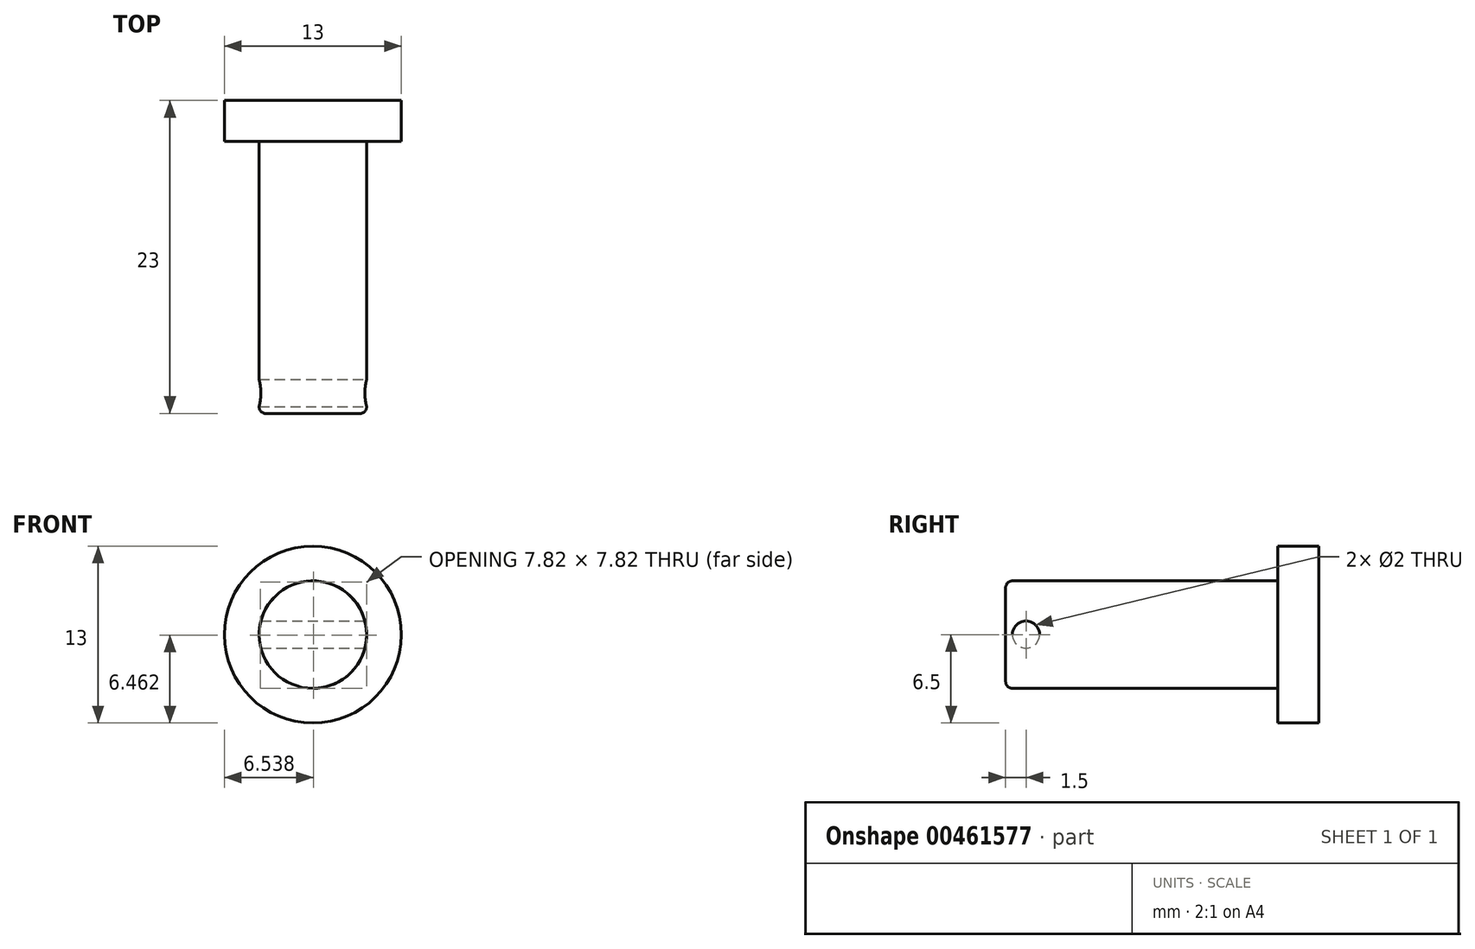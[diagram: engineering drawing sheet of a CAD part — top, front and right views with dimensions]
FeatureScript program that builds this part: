
annotation { "Feature Type Name" : "Feature", "Feature Type Description" : "" }
export const myFeature = defineFeature(function(context is Context, id is Id, definition is map)
    precondition{}
    {
        {
            var Q0;
            Q0=qCreatedBy(makeId("Front.planeOp"),FACE);
            var sketch = newSketch(context, id + "F0", { "sketchPlane" : qUnion([Q0])});
            skCircle(sketch, "E0", {"center": v(0, 0) * mm, "radius": 6.5 * mm});
            skSolve(sketch);
        }
        {
            var Q0;
            Q0=makeQuery(id+"F0.imprint","IMPRINT",FACE,{"disambiguationData":[TD([[makeQuery(id+"F0.imprint","IMPRINT",EDGE,{"derivedFrom":sQuery(id+"F0.wireOp",EDGE,"E0")}),1.0]])]});
            extrude(context, id + "F1", {"entities" : qUnion([Q0]), "depth" : 3 * mm});
        }
        {
            var Q0;
            Q0=makeQuery(id+"F1.opExtrude","CAP_FACE",FACE,{"disambiguationData":[OSD([sQuery(id+"F0.wireOp",EDGE,"E0")])],"isStart":false});
            var sketch = newSketch(context, id + "F2", { "sketchPlane" : qUnion([Q0])});
            skCircle(sketch, "E1", {"center": v(0, 0) * mm, "radius": 3.95 * mm});
            skSolve(sketch);
        }
        {
            var Q0;
            Q0=makeQuery(id+"F2.imprint","IMPRINT",FACE,{"disambiguationData":[TD([[makeQuery(id+"F2.imprint","IMPRINT",EDGE,{"derivedFrom":sQuery(id+"F2.wireOp",EDGE,"E1")}),1.0]])]});
            extrude(context, id + "F3", {"entities" : qUnion([Q0]), "operationType" : NewBodyOperationType.ADD, "depth" : 20 * mm});
        }
        {
            var Q0;
            Q0=qCreatedBy(makeId("Right.planeOp"),FACE);
            cPlane(context, id + "F4", {"entities" : qUnion([Q0]), "cplaneType" : CPlaneType.OFFSET, "offset" : 3.95 * mm, "width" : 150 * mm, "height" : 150 * mm});
        }
        {
            var Q0;
            Q0=qCreatedBy(id+"F4.planeOp",FACE);
            var sketch = newSketch(context, id + "F5", { "sketchPlane" : qUnion([Q0])});
            skCircle(sketch, "E2", {"center": v(-21.5, 0) * mm, "radius": 1 * mm});
            skSolve(sketch);
        }
        {
            var Q0;
            Q0=makeQuery(id+"F5.imprint","IMPRINT",FACE,{"disambiguationData":[TD([[makeQuery(id+"F5.imprint","IMPRINT",EDGE,{"derivedFrom":sQuery(id+"F5.wireOp",EDGE,"E2")}),1.0]])]});
            extrude(context, id + "F6", {"entities" : qUnion([Q0]), "operationType" : NewBodyOperationType.REMOVE, "endBound" : BoundingType.THROUGH_ALL, "oppositeDirection" : true, "depth" : 25 * mm});
        }
        {
            var Q0;
            Q0=makeQuery(id+"F3.opExtrude","CAP_EDGE",EDGE,{"disambiguationData":[OSD([sQuery(id+"F2.wireOp",EDGE,"E1")])],"isStart":false});
            fillet(context, id + "F7", {"entities" : qUnion([Q0]), "radius" : 0.5 * mm, "tangentPropagation" : true, "allowEdgeOverflow" : false});
        }
        {
            var Q0;
            Q0=makeQuery(id+"F1.opExtrude","SWEPT_BODY",BODY,{"disambiguationData":[OSD([sQuery(id+"F0.wireOp",EDGE,"E0")])]});
            transform(context, id + "F8", {"entities" : qUnion([Q0]), "transformType" : TransformType.TRANSLATION_3D, "dx" : 0 * mm, "dy" : 0 * mm, "dz" : 0 * mm, "makeCopy" : true});
        }
    });
